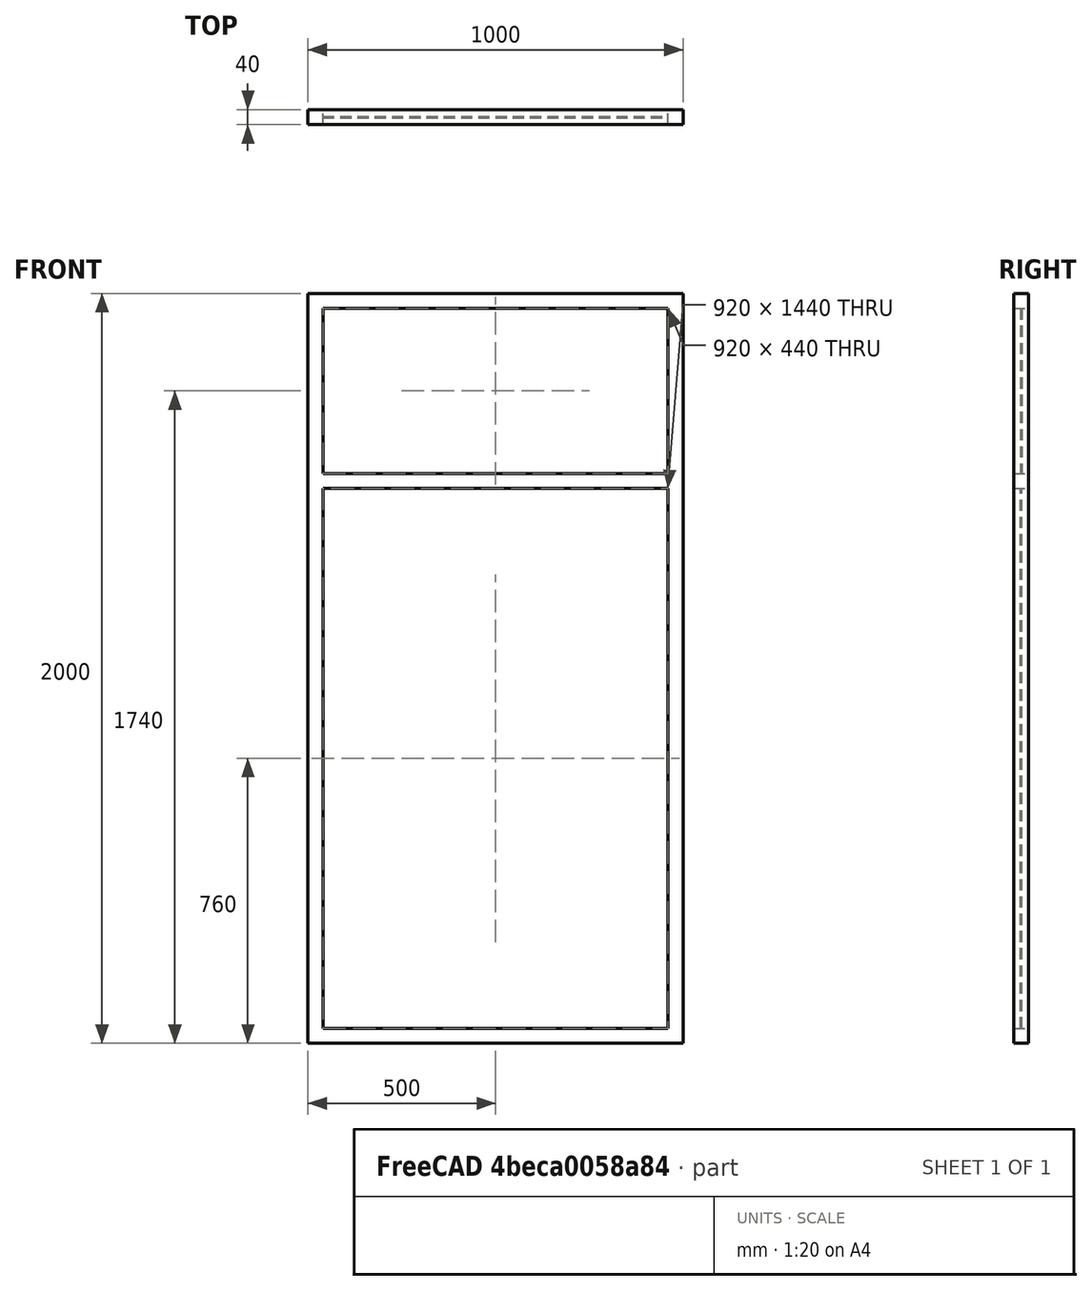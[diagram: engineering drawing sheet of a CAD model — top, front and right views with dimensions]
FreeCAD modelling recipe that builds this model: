
FCSTD DOCUMENT  (FreeCAD 0.16R6704 (Git))
Label: Window with 2 vertical fixed glass
License: CreativeCommons Attribution
LicenseURL: http://creativecommons.org/licenses/by/4.0/
objects: Sketcher::SketchObject×1, Part::FeaturePython×1
note: 2 computed .brp shape members not serialized (recipe doc carries the construction recipe); baked Part::Feature solids carry a one-line shape summary decoded from their .brp

FEATURE [Sketcher::SketchObject] Sketch115  label="Esboço caixilhofixo 2"
  Placement = pos=(0,0,0) rot=(1,0,0;1.5708rad)
  sketch-geometry (18):
    g0: LineSegment StartX=1000 StartY=2000 StartZ=0 EndX=0 EndY=2000 EndZ=0
    g1: LineSegment StartX=0 StartY=2000 StartZ=0 EndX=0 EndY=0 EndZ=0
    g2: LineSegment StartX=0 StartY=0 StartZ=0 EndX=1000 EndY=0 EndZ=0
    g3: LineSegment StartX=1000 StartY=0 StartZ=0 EndX=1000 EndY=2000 EndZ=0
    g4: LineSegment StartX=40 StartY=1960 StartZ=0 EndX=960 EndY=1960 EndZ=0
    g5: LineSegment StartX=960 StartY=1960 StartZ=0 EndX=960 EndY=1520 EndZ=0
    g6: LineSegment StartX=960 StartY=1520 StartZ=0 EndX=40 EndY=1520 EndZ=0
    g7: LineSegment StartX=40 StartY=1520 StartZ=0 EndX=40 EndY=1960 EndZ=0
    g8: LineSegment StartX=40 StartY=40 StartZ=0 EndX=960 EndY=40 EndZ=0
    g9: LineSegment StartX=960 StartY=40 StartZ=0 EndX=960 EndY=1480 EndZ=0
    g10: LineSegment StartX=960 StartY=1480 StartZ=0 EndX=40 EndY=1480 EndZ=0
    g11: LineSegment StartX=40 StartY=1480 StartZ=0 EndX=40 EndY=40 EndZ=0
    g12: LineSegment [constr] StartX=-286.136 StartY=1500 StartZ=0 EndX=1289.44 EndY=1500 EndZ=0
    g13: LineSegment [constr] StartX=125.706 StartY=2000 StartZ=0 EndX=125.706 EndY=1960 EndZ=0
    g14: LineSegment [constr] StartX=0 StartY=1880.94 StartZ=0 EndX=40 EndY=1880.94 EndZ=0
    g15: LineSegment [constr] StartX=282.161 StartY=1520 StartZ=0 EndX=282.161 EndY=1480 EndZ=0
    g16: LineSegment [constr] StartX=960 StartY=1637.72 StartZ=0 EndX=1000 EndY=1637.72 EndZ=0
    g17: LineSegment [constr] StartX=516.273 StartY=40 StartZ=0 EndX=516.273 EndY=0 EndZ=0
  constraints (51):
    c: Coincident(g0,g1)
    c: Horizontal(g0)
    c: Coincident(g1,g2)
    c: Vertical(g1)
    c: Coincident(g2,g3)
    c: Horizontal(g2)
    c: Coincident(g3,g0)
    c: Coincident(g4,g5)
    c: Horizontal(g4)
    c: Coincident(g5,g6)
    c: Vertical(g5)
    c: Coincident(g6,g7)
    c: Horizontal(g6)
    c: Coincident(g7,g4)
    c: Coincident(g8,g9)
    c: Horizontal(g8)
    c: Coincident(g9,g10)
    c: Vertical(g9)
    c: Coincident(g10,g11)
    c: Horizontal(g10)
    c: Coincident(g11,g8)
    c: DistanceX(g0,g4) = 40  'Montantes'
    c: DistanceX(g6,g10) = 0  'Constraint31'
    c: DistanceX(g5,g9) = 0  'Constraint25'
    c: DistanceX(g0,g0) = 1000  'Largura do vão'
    c: DistanceY(g2,g0) = 2000  'Altura vão'
    c: Symmetric(g10,g6,g12)  'Constraint40'
    c: DistanceY(g12,g0) = 500  'Altura parte superior'
    c: Coincident(g1,g-1)  'Constraint41'
    c: Vertical(g7)  'Constraint30'
    c: Vertical(g3)  'Constraint34'
    c: Vertical(g11)  'Constraint33'
    c: PointOnObject(g13,g0)
    c: PointOnObject(g13,g4)
    c: PointOnObject(g14,g1)
    c: PointOnObject(g14,g7)
    c: PointOnObject(g16,g5)
    c: PointOnObject(g16,g3)
    c: PointOnObject(g15,g6)
    c: PointOnObject(g15,g10)
    c: PointOnObject(g17,g8)
    c: PointOnObject(g17,g2)
    c: Equal(g14,g13)
    c: Equal(g13,g16)
    c: Equal(g16,g15)
    c: Equal(g15,g17)
    c: Angle(g13) = -1.5708
    c: Angle(g14) = 0
    c: Angle(g15) = -1.5708
    c: Angle(g16) = 0
    c: Angle(g17) = -1.5708
FEATURE [Part::FeaturePython] Window083  label="Window with 2 vertical fixed glass"  # WARN: FeaturePython — macro-defined, semantics opaque (R4)
  Base = -> Sketch115
  Height = 0
  HoleDepth = 0
  MoveWithHost = true
  Normal = (0,1,0)
  Preset = 0
  Role = 0
  Width = 0
  WindowParts = Montante | Frame | Wire0,Wire1,Wire2 | 40.0 | 0.0 | Vidro 1 | Glass panel | Wire1 | 4.0 | 18.0 | Vidro 2 | Glass panel | Wire2 | 4.0 | 18.0
